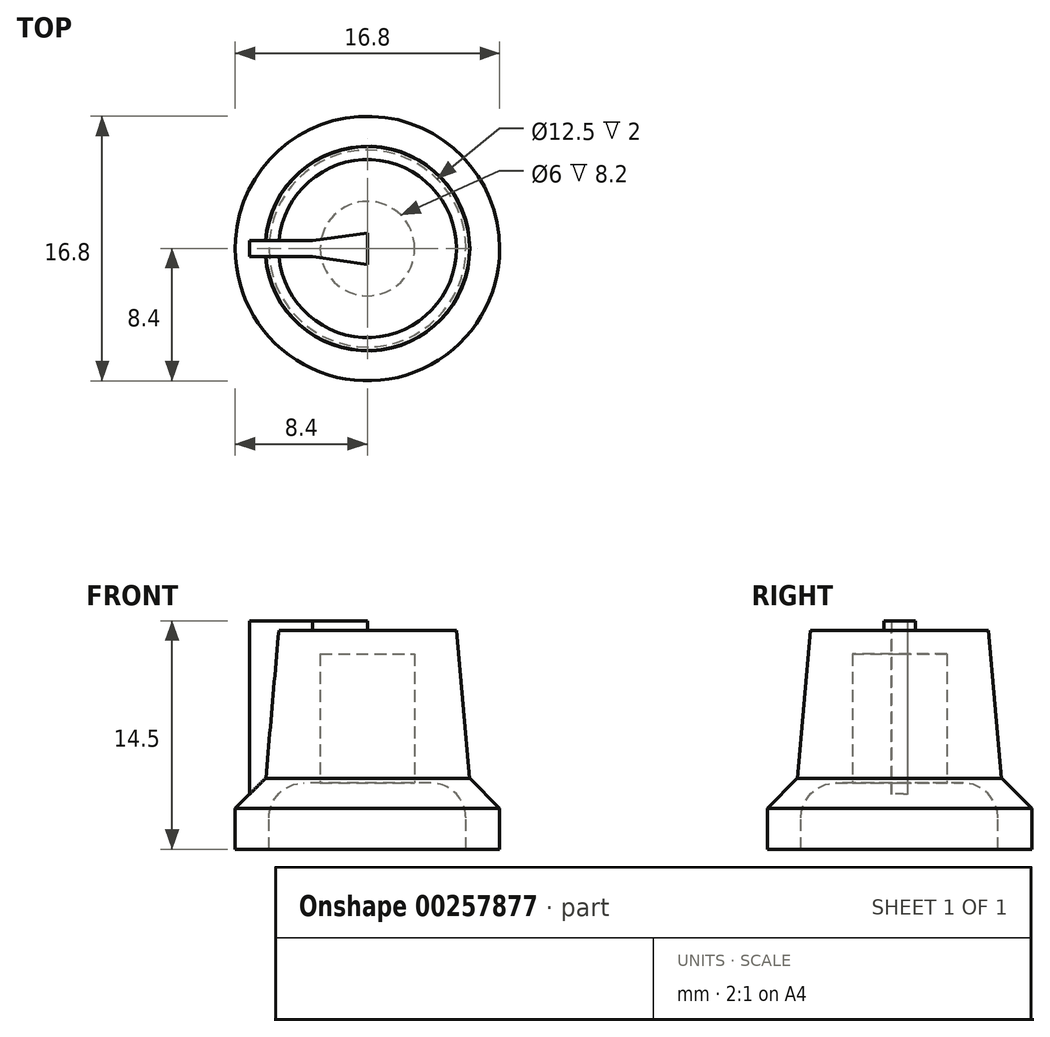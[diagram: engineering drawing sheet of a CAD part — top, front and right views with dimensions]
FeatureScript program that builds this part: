
annotation { "Feature Type Name" : "Feature", "Feature Type Description" : "" }
export const myFeature = defineFeature(function(context is Context, id is Id, definition is map)
    precondition{}
    {
        {
            var Q0;
            Q0=qCreatedBy(makeId("Top.planeOp"),FACE);
            var sketch = newSketch(context, id + "F0", { "sketchPlane" : qUnion([Q0])});
            skCircle(sketch, "E0", {"center": v(0, 0) * mm, "radius": 8.4 * mm});
            skSolve(sketch);
        }
        {
            var Q0;
            Q0=makeQuery(id+"F0.imprint","IMPRINT",FACE,{"disambiguationData":[TD([[makeQuery(id+"F0.imprint","IMPRINT",EDGE,{"derivedFrom":sQuery(id+"F0.wireOp",EDGE,"E0")}),1.0]])]});
            extrude(context, id + "F1", {"entities" : qUnion([Q0]), "depth" : 4.5 * mm});
        }
        {
            var Q0;
            Q0=qCreatedBy(makeId("Top.planeOp"),FACE);
            cPlane(context, id + "F2", {"entities" : qUnion([Q0]), "cplaneType" : CPlaneType.OFFSET, "offset" : 13.9 * mm, "width" : 150 * mm, "height" : 150 * mm});
        }
        {
            var Q0;
            Q0=qCreatedBy(id+"F2.planeOp",FACE);
            var sketch = newSketch(context, id + "F3", { "sketchPlane" : qUnion([Q0])});
            skCircle(sketch, "E1", {"center": v(0, 0) * mm, "radius": 5.65 * mm});
            skSolve(sketch);
        }
        {
            var Q0;
            Q0=makeQuery(id+"F3.imprint","IMPRINT",FACE,{"disambiguationData":[TD([[makeQuery(id+"F3.imprint","IMPRINT",EDGE,{"derivedFrom":sQuery(id+"F3.wireOp",EDGE,"E1")}),1.0]])]});
            var Q1;
            Q1=makeQuery(id+"F1.opExtrude","CAP_FACE",FACE,{"disambiguationData":[OSD([sQuery(id+"F0.wireOp",EDGE,"E0")])],"isStart":false});
            extrude(context, id + "F4", {"entities" : qUnion([Q0]), "operationType" : NewBodyOperationType.ADD, "endBound" : BoundingType.UP_TO_SURFACE, "oppositeDirection" : true, "endBoundEntityFace" : qUnion([Q1]), "depth" : 25 * mm, "hasDraft" : true, "draftAngle" : 5 * degree});
        }
        {
            var Q0;
            Q0=makeQuery(id+"F1.opExtrude","CAP_EDGE",EDGE,{"disambiguationData":[OSD([sQuery(id+"F0.wireOp",EDGE,"E0")])],"isStart":false});
            chamfer(context, id + "F5", {"entities" : qUnion([Q0]), "width" : 1.9 * mm, "tangentPropagation" : true});
        }
        {
            var Q0;
            Q0=makeQuery(id+"F4.opExtrude","CAP_FACE",FACE,{"disambiguationData":[OSD([sQuery(id+"F3.wireOp",EDGE,"E1")])],"isStart":true});
            var sketch = newSketch(context, id + "F6", { "sketchPlane" : qUnion([Q0])});
            skLineSegment(sketch, "E2", {"start": v(0, 1) * mm, "end": v(0, -1) * mm});
            skLineSegment(sketch, "E3", {"start": v(0, -1) * mm, "end": v(-3.5, -0.5) * mm});
            skLineSegment(sketch, "E4", {"start": v(-3.5, -0.5) * mm, "end": v(-7.5, -0.5) * mm});
            skLineSegment(sketch, "E5", {"start": v(-7.5, -0.5) * mm, "end": v(-7.5, 0.5) * mm});
            skLineSegment(sketch, "E6", {"start": v(-7.5, 0.5) * mm, "end": v(-3.5, 0.5) * mm});
            skLineSegment(sketch, "E7", {"start": v(-3.5, 0.5) * mm, "end": v(0, 1) * mm});
            skSolve(sketch);
        }
        {
            var Q0;
            {var subQ0=sQuery(id+"F6.wireOp",EDGE,"E5");Q0=makeQuery(id+"F6.imprint","IMPRINT",FACE,{"disambiguationData":[TD([[makeQuery(id+"F6.imprint","IMPRINT",EDGE,{"derivedFrom":subQ0}),-1.0]])]});}
            var Q1;
            Q1=makeQuery(id+"F6.imprint","IMPRINT",FACE,{"disambiguationData":[TD([[makeQuery(id+"F6.imprint","IMPRINT",EDGE,{"derivedFrom":sQuery(id+"F6.wireOp",EDGE,"E2")}),-1.0]])]});
            extrude(context, id + "F7", {"entities" : qUnion([Q0, Q1]), "depth" : (14.5 - 13.9) * mm});
        }
        {
            var Q0;
            Q0=makeQuery(id+"F7.opExtrude","CAP_FACE",FACE,{"disambiguationData":[OSD([sQuery(id+"F6.wireOp",EDGE,"E2"),sQuery(id+"F6.wireOp",EDGE,"E3"),sQuery(id+"F6.wireOp",EDGE,"E4"),sQuery(id+"F6.wireOp",EDGE,"E5"),sQuery(id+"F6.wireOp",EDGE,"E6"),sQuery(id+"F6.wireOp",EDGE,"E7")])],"isStart":true});
            var sketch = newSketch(context, id + "F8", { "sketchPlane" : qUnion([Q0])});
            skLineSegment(sketch, "E8.bottom", {"start": v(-7.5, 0.5) * mm, "end": v(-5.5, 0.5) * mm});
            skLineSegment(sketch, "E8.top", {"start": v(-7.5, -0.5) * mm, "end": v(-5.5, -0.5) * mm});
            skLineSegment(sketch, "E8.left", {"start": v(-7.5, 0.5) * mm, "end": v(-7.5, -0.5) * mm});
            skLineSegment(sketch, "E8.right", {"start": v(-5.5, 0.5) * mm, "end": v(-5.5, -0.5) * mm});
            skSolve(sketch);
        }
        {
            var Q0;
            Q0=makeQuery(id+"F8.imprint","IMPRINT",FACE,{"disambiguationData":[TD([[makeQuery(id+"F8.imprint","IMPRINT",EDGE,{"derivedFrom":sQuery(id+"F8.wireOp",EDGE,"E8.bottom")}),1.0]])]});
            extrude(context, id + "F9", {"entities" : qUnion([Q0]), "operationType" : NewBodyOperationType.ADD, "depth" : 10.5 * mm});
        }
        {
            var Q0;
            Q0=qCreatedBy(makeId("Right.planeOp"),FACE);
            var sketch = newSketch(context, id + "F10", { "sketchPlane" : qUnion([Q0])});
            skLineSegment(sketch, "E9", {"start": v(-6.25, 0) * mm, "end": v(-6.25, 2) * mm});
            skLineSegment(sketch, "E10", {"start": v(0, 0) * mm, "end": v(0, 4.2) * mm});
            skLineSegment(sketch, "E11", {"start": v(-6.25, 0) * mm, "end": v(0, 0) * mm});
            skLineSegment(sketch, "E12", {"start": v(0, 4.2) * mm, "end": v(-4.04, 4.2) * mm});
            skArc(sketch, "E13", {"start": v(-4.04, 4.2) * mm, "mid": v(-5.6, 3.56) * mm, "end": v(-6.25, 2) * mm});
            skSolve(sketch);
        }
        {
            var Q0;
            Q0=makeQuery(id+"F10.imprint","IMPRINT",FACE,{"disambiguationData":[TD([[makeQuery(id+"F10.imprint","IMPRINT",EDGE,{"derivedFrom":sQuery(id+"F10.wireOp",EDGE,"E9")}),-1.0]])]});
            var Q1;
            Q1=sQuery(id+"F10.wireOp",EDGE,"E13");
            var Q2;
            Q2=sQuery(id+"F10.wireOp",EDGE,"E12");
            var Q3;
            Q3=sQuery(id+"F10.wireOp",EDGE,"E10");
            revolve(context, id + "F11", {"operationType" : NewBodyOperationType.REMOVE, "entities" : qUnion([Q0]), "surfaceEntities" : qUnion([Q1, Q2]), "axis" : qUnion([Q3]), "revolveType" : RevolveType.FULL, "oppositeDirection" : true});
        }
        {
            var Q0;
            Q0=makeQuery(id+"F11.boolean.opBoolean","COPY",FACE,{"derivedFrom":makeQuery(id+"F11.opRevolve","SWEPT_FACE",FACE,{"disambiguationData":[OSD([sQuery(id+"F10.wireOp",EDGE,"E12")])]})});
            var sketch = newSketch(context, id + "F12", { "sketchPlane" : qUnion([Q0])});
            skCircle(sketch, "E14", {"center": v(0, 0) * mm, "radius": 3 * mm});
            skSolve(sketch);
        }
        {
            var Q0;
            Q0 = qSketchRegion(id + "F12", true);
            extrude(context, id + "F13", {"entities" : qUnion([Q0]), "operationType" : NewBodyOperationType.REMOVE, "oppositeDirection" : true, "depth" : (12.4 - 4.2) * mm});
        }
    });
